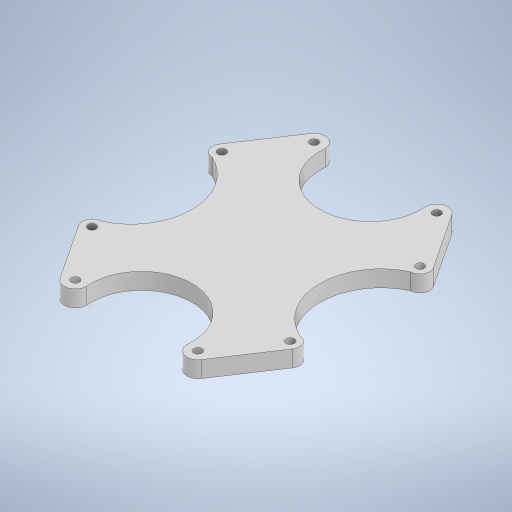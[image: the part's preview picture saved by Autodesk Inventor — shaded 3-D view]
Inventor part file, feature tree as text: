
AUTODESK INVENTOR PART (.ipt)
format: ipt  version: 2023 (Build 270158000, 158)  size: 306,176 bytes
history: native  units: in
note: dims shown in document units (in); Inventor stores cm internally (conversion verified against a paired STEP export)
features: sketch x2, plane x1, extrude x1
ambient origin geometry x8: Origin, YZ Plane, XZ Plane, XY Plane, X Axis, Y Axis, Z Axis, Center Point
bodies: Body1 (feature_tree)
feature tree (4):
  sketch  "Sketch1"  dims[d2=2.1654in d10=0.315in]
  plane  "Work Plane1"
  extrude  "Extrusion1"  Depth=0.315in
  sketch  "Sketch6"  dims[d11=0.315in d12=0.315in d13=0.315in d14=0.2756in d15=0.2756in d16=0.2756in d17=0.2756in d18=0.2362in d19=0.0in d5=0.0197in d6=0.0344in d7=0.0197in d8=0.0344in d20=0.0in d21=0.0in d22=0.0in d23=0.0in d24=0.0in d25=0.0in]
